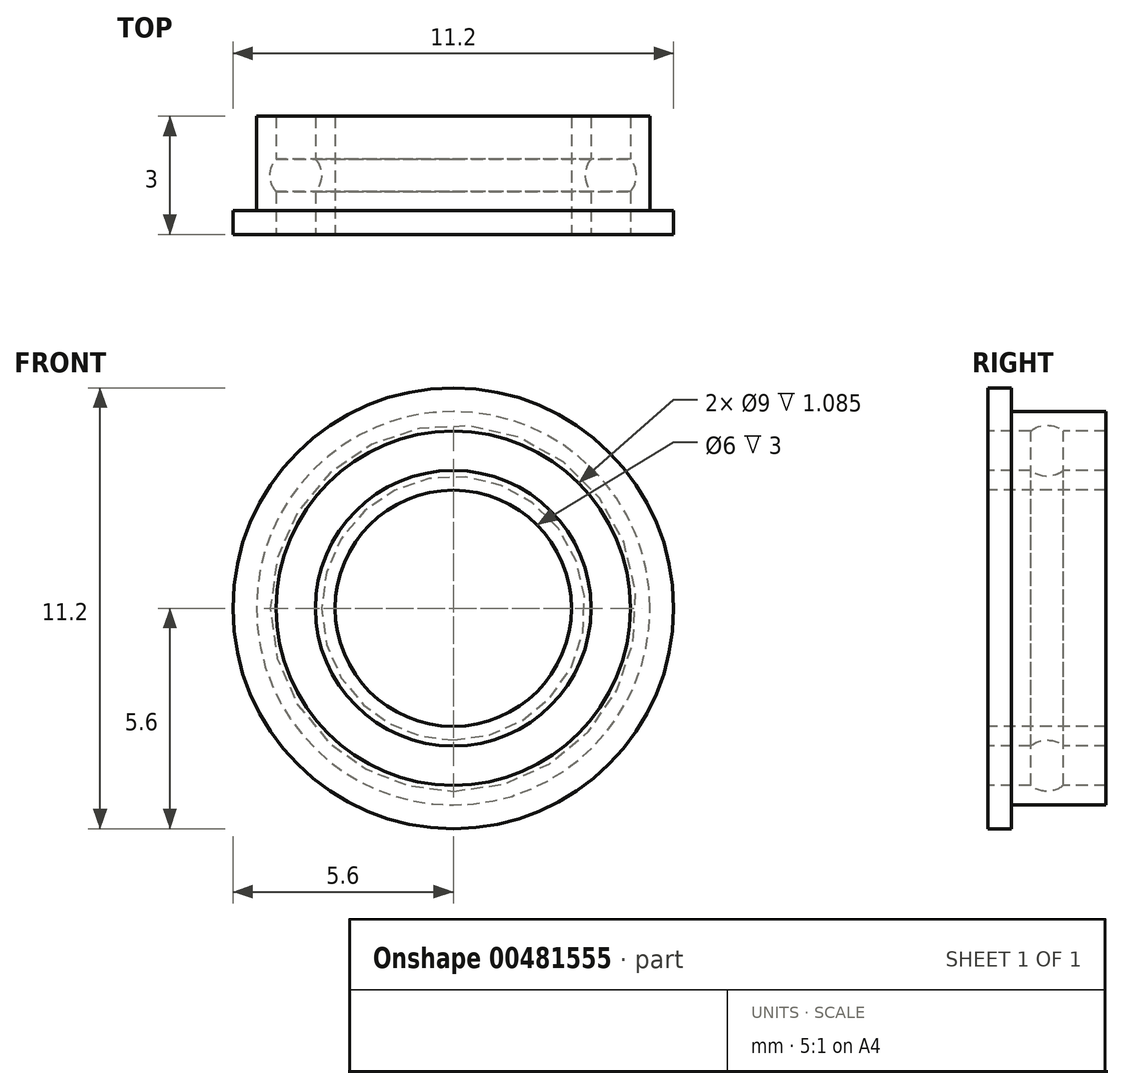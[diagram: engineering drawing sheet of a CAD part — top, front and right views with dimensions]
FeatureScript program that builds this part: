
annotation { "Feature Type Name" : "Feature", "Feature Type Description" : "" }
export const myFeature = defineFeature(function(context is Context, id is Id, definition is map)
    precondition{}
    {
        {
            var Q0;
            Q0=qCreatedBy(makeId("Right.planeOp"),FACE);
            var sketch = newSketch(context, id + "F0", { "sketchPlane" : qUnion([Q0])});
            skLineSegment(sketch, "E0", {"start": v(-1.5, 0) * mm, "end": v(1.5, 0) * mm, "construction": true});
            skLineSegment(sketch, "E1", {"start": v(-1.5, 5.6) * mm, "end": v(-1.5, 3) * mm});
            skLineSegment(sketch, "E2", {"start": v(-1.5, 3) * mm, "end": v(1.5, 3) * mm});
            skLineSegment(sketch, "E3", {"start": v(1.5, 3) * mm, "end": v(1.5, 5) * mm});
            skLineSegment(sketch, "E4", {"start": v(1.5, 5) * mm, "end": v(-0.9, 5) * mm});
            skLineSegment(sketch, "E5", {"start": v(-0.9, 5) * mm, "end": v(-0.9, 5.6) * mm});
            skLineSegment(sketch, "E6", {"start": v(-0.9, 5.6) * mm, "end": v(-1.5, 5.6) * mm});
            skCircle(sketch, "E7", {"center": v(0, 4) * mm, "radius": 0.65 * mm});
            skLineSegment(sketch, "E8", {"start": v(0, 0) * mm, "end": v(0, 4) * mm, "construction": true});
            skLineSegment(sketch, "E9", {"start": v(1.5, 4) * mm, "end": v(0, 4) * mm, "construction": true});
            skLineSegment(sketch, "E10", {"start": v(-1.5, 4.5) * mm, "end": v(1.5, 4.5) * mm});
            skLineSegment(sketch, "E11", {"start": v(1.5, 3.5) * mm, "end": v(-1.5, 3.5) * mm});
            skSolve(sketch);
        }
        {
            var Q0;
            {var subQ1=sQuery(id+"F0.wireOp",EDGE,"E2");Q0=makeQuery(id+"F0.imprint","IMPRINT",FACE,{"disambiguationData":[TD([[makeQuery(id+"F0.imprint","IMPRINT",EDGE,{"derivedFrom":subQ1}),1.0]])]});}
            var Q1;
            {var subQ0=sQuery(id+"F0.wireOp",EDGE,"E4");Q1=makeQuery(id+"F0.imprint","IMPRINT",FACE,{"disambiguationData":[TD([[makeQuery(id+"F0.imprint","IMPRINT",EDGE,{"derivedFrom":subQ0}),1.0]])]});}
            var Q2;
            Q2=sQuery(id+"F0.wireOp",EDGE,"E0");
            revolve(context, id + "F1", {"entities" : qUnion([Q0, Q1]), "axis" : qUnion([Q2]), "revolveType" : RevolveType.FULL});
        }
    });
